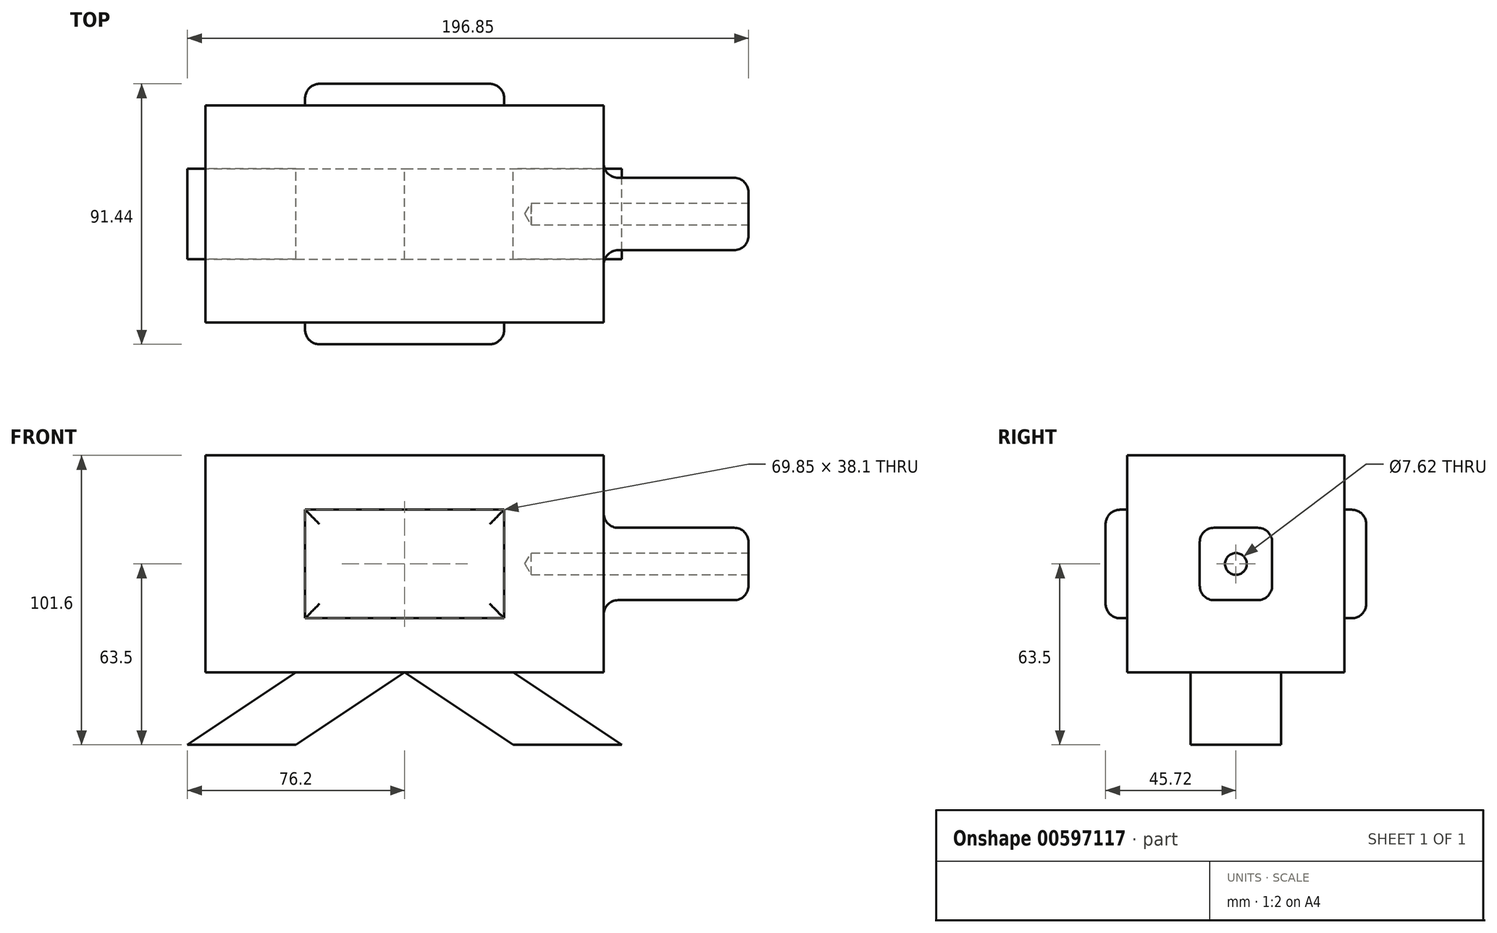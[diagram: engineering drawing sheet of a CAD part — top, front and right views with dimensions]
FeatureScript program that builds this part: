
annotation { "Feature Type Name" : "Feature", "Feature Type Description" : "" }
export const myFeature = defineFeature(function(context is Context, id is Id, definition is map)
    precondition{}
    {
        {
            var Q0;
            Q0=qCreatedBy(makeId("Top.planeOp"),FACE);
            var sketch = newSketch(context, id + "F0", { "sketchPlane" : qUnion([Q0])});
            skLineSegment(sketch, "E0.bottom", {"start": v(69.85, 38.1) * mm, "end": v(-69.85, 38.1) * mm});
            skLineSegment(sketch, "E0.top", {"start": v(69.85, -38.1) * mm, "end": v(-69.85, -38.1) * mm});
            skLineSegment(sketch, "E0.left", {"start": v(69.85, 38.1) * mm, "end": v(69.85, -38.1) * mm});
            skLineSegment(sketch, "E0.right", {"start": v(-69.85, 38.1) * mm, "end": v(-69.85, -38.1) * mm});
            skPoint(sketch, "E0.middle", {"position": v(0, 0) * mm});
            skSolve(sketch);
        }
        {
            var Q0;
            Q0=makeQuery(id+"F0.imprint","IMPRINT",FACE,{"disambiguationData":[TD([[makeQuery(id+"F0.imprint","IMPRINT",EDGE,{"derivedFrom":sQuery(id+"F0.wireOp",EDGE,"E0.bottom")}),1.0]])]});
            extrude(context, id + "F1", {"entities" : qUnion([Q0]), "depth" : 76.2 * mm, "offsetDistance" : 25.4 * mm});
        }
        {
            var Q0;
            Q0=makeQuery(id+"F1.opExtrude","SWEPT_FACE",FACE,{"disambiguationData":[OSD([sQuery(id+"F0.wireOp",EDGE,"E0.left")])]});
            var sketch = newSketch(context, id + "F2", { "sketchPlane" : qUnion([Q0])});
            skLineSegment(sketch, "E1", {"start": v(-38.1, 76.2) * mm, "end": v(38.1, 0) * mm});
            skLineSegment(sketch, "E2", {"start": v(38.1, 0) * mm, "end": v(-38.1, 0) * mm});
            skLineSegment(sketch, "E3", {"start": v(-38.1, 0) * mm, "end": v(38.1, 76.2) * mm});
            skLineSegment(sketch, "E4", {"start": v(0, 38.1) * mm, "end": v(0, 50.8) * mm});
            skPoint(sketch, "E4.endSnap0", {"position": v(0, 38.1) * mm});
            skLineSegment(sketch, "E5", {"start": v(0, 38.1) * mm, "end": v(-12.7, 38.1) * mm});
            skLineSegment(sketch, "E6", {"start": v(0, 38.1) * mm, "end": v(12.7, 38.1) * mm});
            skLineSegment(sketch, "E7", {"start": v(0, 38.1) * mm, "end": v(0, 25.4) * mm});
            skLineSegment(sketch, "E8.bottom", {"start": v(-12.7, 50.8) * mm, "end": v(12.7, 50.8) * mm});
            skLineSegment(sketch, "E8.top", {"start": v(-12.7, 25.4) * mm, "end": v(12.7, 25.4) * mm});
            skLineSegment(sketch, "E8.left", {"start": v(-12.7, 50.8) * mm, "end": v(-12.7, 25.4) * mm});
            skLineSegment(sketch, "E8.right", {"start": v(12.7, 50.8) * mm, "end": v(12.7, 25.4) * mm});
            skSolve(sketch);
        }
        {
            var Q0;
            {var subQ0=sQuery(id+"F2.wireOp",EDGE,"E4");Q0=makeQuery(id+"F2.imprint","IMPRINT",FACE,{"disambiguationData":[TD([[makeQuery(id+"F2.imprint","IMPRINT",EDGE,{"derivedFrom":subQ0}),-1.0]])]});}
            var Q1;
            {var subQ0=sQuery(id+"F2.wireOp",EDGE,"E6");Q1=makeQuery(id+"F2.imprint","IMPRINT",FACE,{"disambiguationData":[TD([[makeQuery(id+"F2.imprint","IMPRINT",EDGE,{"derivedFrom":subQ0}),1.0]])]});}
            var Q2;
            {var subQ0=sQuery(id+"F2.wireOp",EDGE,"E6");Q2=makeQuery(id+"F2.imprint","IMPRINT",FACE,{"disambiguationData":[TD([[makeQuery(id+"F2.imprint","IMPRINT",EDGE,{"derivedFrom":subQ0}),-1.0]])]});}
            var Q3;
            {var subQ0=sQuery(id+"F2.wireOp",EDGE,"E7");Q3=makeQuery(id+"F2.imprint","IMPRINT",FACE,{"disambiguationData":[TD([[makeQuery(id+"F2.imprint","IMPRINT",EDGE,{"derivedFrom":subQ0}),1.0]])]});}
            var Q4;
            {var subQ0=sQuery(id+"F2.wireOp",EDGE,"E7");Q4=makeQuery(id+"F2.imprint","IMPRINT",FACE,{"disambiguationData":[TD([[makeQuery(id+"F2.imprint","IMPRINT",EDGE,{"derivedFrom":subQ0}),-1.0]])]});}
            var Q5;
            {var subQ0=sQuery(id+"F2.wireOp",EDGE,"E5");Q5=makeQuery(id+"F2.imprint","IMPRINT",FACE,{"disambiguationData":[TD([[makeQuery(id+"F2.imprint","IMPRINT",EDGE,{"derivedFrom":subQ0}),1.0]])]});}
            var Q6;
            {var subQ0=sQuery(id+"F2.wireOp",EDGE,"E4");Q6=makeQuery(id+"F2.imprint","IMPRINT",FACE,{"disambiguationData":[TD([[makeQuery(id+"F2.imprint","IMPRINT",EDGE,{"derivedFrom":subQ0}),1.0]])]});}
            var Q7;
            {var subQ0=sQuery(id+"F2.wireOp",EDGE,"E5");Q7=makeQuery(id+"F2.imprint","IMPRINT",FACE,{"disambiguationData":[TD([[makeQuery(id+"F2.imprint","IMPRINT",EDGE,{"derivedFrom":subQ0}),-1.0]])]});}
            extrude(context, id + "F3", {"entities" : qUnion([Q0, Q1, Q2, Q3, Q4, Q5, Q6, Q7]), "operationType" : NewBodyOperationType.ADD, "depth" : 50.8 * mm, "offsetDistance" : 25.4 * mm});
        }
        {
            var Q0;
            Q0=makeQuery(id+"F1.opExtrude","SWEPT_FACE",FACE,{"disambiguationData":[OSD([sQuery(id+"F0.wireOp",EDGE,"E0.top")])]});
            var sketch = newSketch(context, id + "F4", { "sketchPlane" : qUnion([Q0])});
            skLineSegment(sketch, "E9", {"start": v(-69.85, 76.2) * mm, "end": v(69.85, 0) * mm});
            skLineSegment(sketch, "E10", {"start": v(69.85, 0) * mm, "end": v(69.85, 76.2) * mm});
            skLineSegment(sketch, "E11", {"start": v(69.85, 76.2) * mm, "end": v(-69.85, 0) * mm});
            skLineSegment(sketch, "E12.bottom", {"start": v(34.93, 57.15) * mm, "end": v(-34.93, 57.15) * mm});
            skLineSegment(sketch, "E12.top", {"start": v(34.93, 19.05) * mm, "end": v(-34.93, 19.05) * mm});
            skLineSegment(sketch, "E12.left", {"start": v(34.93, 57.15) * mm, "end": v(34.93, 19.05) * mm});
            skLineSegment(sketch, "E12.right", {"start": v(-34.93, 57.15) * mm, "end": v(-34.93, 19.05) * mm});
            skPoint(sketch, "E12.middle", {"position": v(0, 38.1) * mm});
            skSolve(sketch);
        }
        {
            var Q0;
            Q0=makeQuery(id+"F1.opExtrude","SWEPT_FACE",FACE,{"disambiguationData":[OSD([sQuery(id+"F0.wireOp",EDGE,"E0.bottom")])]});
            var sketch = newSketch(context, id + "F5", { "sketchPlane" : qUnion([Q0])});
            skLineSegment(sketch, "E13", {"start": v(-69.85, 76.2) * mm, "end": v(69.85, 0) * mm});
            skLineSegment(sketch, "E14", {"start": v(69.85, 0) * mm, "end": v(-69.85, 0) * mm});
            skLineSegment(sketch, "E15", {"start": v(-69.85, 0) * mm, "end": v(69.85, 76.2) * mm});
            skLineSegment(sketch, "E16.bottom", {"start": v(34.93, 57.15) * mm, "end": v(-34.93, 57.15) * mm});
            skLineSegment(sketch, "E16.top", {"start": v(34.93, 19.05) * mm, "end": v(-34.93, 19.05) * mm});
            skLineSegment(sketch, "E16.left", {"start": v(34.93, 57.15) * mm, "end": v(34.93, 19.05) * mm});
            skLineSegment(sketch, "E16.right", {"start": v(-34.93, 57.15) * mm, "end": v(-34.93, 19.05) * mm});
            skPoint(sketch, "E16.middle", {"position": v(0, 38.1) * mm});
            skSolve(sketch);
        }
        {
            var Q0;
            {var subQ0=sQuery(id+"F5.wireOp",EDGE,"E16.bottom");Q0=makeQuery(id+"F5.imprint","IMPRINT",FACE,{"disambiguationData":[TD([[makeQuery(id+"F5.imprint","IMPRINT",EDGE,{"derivedFrom":subQ0}),1.0]])]});}
            var Q1;
            {var subQ0=sQuery(id+"F5.wireOp",EDGE,"E16.right");Q1=makeQuery(id+"F5.imprint","IMPRINT",FACE,{"disambiguationData":[TD([[makeQuery(id+"F5.imprint","IMPRINT",EDGE,{"derivedFrom":subQ0}),1.0]])]});}
            var Q2;
            {var subQ0=sQuery(id+"F5.wireOp",EDGE,"E16.left");Q2=makeQuery(id+"F5.imprint","IMPRINT",FACE,{"disambiguationData":[TD([[makeQuery(id+"F5.imprint","IMPRINT",EDGE,{"derivedFrom":subQ0}),-1.0]])]});}
            var Q3;
            {var subQ0=sQuery(id+"F5.wireOp",EDGE,"E16.top");Q3=makeQuery(id+"F5.imprint","IMPRINT",FACE,{"disambiguationData":[TD([[makeQuery(id+"F5.imprint","IMPRINT",EDGE,{"derivedFrom":subQ0}),-1.0]])]});}
            extrude(context, id + "F6", {"entities" : qUnion([Q0, Q1, Q2, Q3]), "operationType" : NewBodyOperationType.ADD, "depth" : 7.62 * mm, "offsetDistance" : 25.4 * mm});
        }
        {
            var Q0;
            {var subQ0=sQuery(id+"F4.wireOp",EDGE,"E12.bottom");Q0=makeQuery(id+"F4.imprint","IMPRINT",FACE,{"disambiguationData":[TD([[makeQuery(id+"F4.imprint","IMPRINT",EDGE,{"derivedFrom":subQ0}),1.0]])]});}
            var Q1;
            {var subQ0=sQuery(id+"F4.wireOp",EDGE,"E12.right");Q1=makeQuery(id+"F4.imprint","IMPRINT",FACE,{"disambiguationData":[TD([[makeQuery(id+"F4.imprint","IMPRINT",EDGE,{"derivedFrom":subQ0}),1.0]])]});}
            var Q2;
            {var subQ0=sQuery(id+"F4.wireOp",EDGE,"E12.top");Q2=makeQuery(id+"F4.imprint","IMPRINT",FACE,{"disambiguationData":[TD([[makeQuery(id+"F4.imprint","IMPRINT",EDGE,{"derivedFrom":subQ0}),-1.0]])]});}
            var Q3;
            {var subQ0=sQuery(id+"F4.wireOp",EDGE,"E12.left");Q3=makeQuery(id+"F4.imprint","IMPRINT",FACE,{"disambiguationData":[TD([[makeQuery(id+"F4.imprint","IMPRINT",EDGE,{"derivedFrom":subQ0}),-1.0]])]});}
            extrude(context, id + "F7", {"entities" : qUnion([Q0, Q1, Q2, Q3]), "operationType" : NewBodyOperationType.ADD, "depth" : 7.62 * mm, "offsetDistance" : 25.4 * mm});
        }
        {
            var Q0;
            Q0=makeQuery(id+"F1.opExtrude","CAP_FACE",FACE,{"disambiguationData":[OSD([sQuery(id+"F0.wireOp",EDGE,"E0.bottom"),sQuery(id+"F0.wireOp",EDGE,"E0.top"),sQuery(id+"F0.wireOp",EDGE,"E0.left"),sQuery(id+"F0.wireOp",EDGE,"E0.right")])],"isStart":true});
            var sketch = newSketch(context, id + "F8", { "sketchPlane" : qUnion([Q0])});
            skLineSegment(sketch, "E17.bottom", {"start": v(-38.1, 15.88) * mm, "end": v(38.1, 15.88) * mm});
            skLineSegment(sketch, "E17.top", {"start": v(-38.1, -15.88) * mm, "end": v(38.1, -15.88) * mm});
            skLineSegment(sketch, "E17.left", {"start": v(-38.1, 15.88) * mm, "end": v(-38.1, -15.87) * mm});
            skLineSegment(sketch, "E17.right", {"start": v(38.1, 15.88) * mm, "end": v(38.1, -15.87) * mm});
            skPoint(sketch, "E17.middle", {"position": v(0, 0) * mm});
            skLineSegment(sketch, "E18", {"start": v(0, 15.88) * mm, "end": v(0, -15.88) * mm});
            skSolve(sketch);
        }
        {
            var Q0;
            {var subQ0=sQuery(id+"F8.wireOp",EDGE,"E17.right");Q0=makeQuery(id+"F8.imprint","IMPRINT",FACE,{"disambiguationData":[TD([[makeQuery(id+"F8.imprint","IMPRINT",EDGE,{"derivedFrom":subQ0}),-1.0]])]});}
            cPlane(context, id + "F9", {"entities" : qUnion([Q0]), "cplaneType" : CPlaneType.OFFSET, "offset" : 25.4 * mm, "width" : 152.4 * mm, "height" : 152.4 * mm});
        }
        {
            var Q0;
            Q0=qCreatedBy(id+"F9.planeOp",FACE);
            var sketch = newSketch(context, id + "F10", { "sketchPlane" : qUnion([Q0])});
            skLineSegment(sketch, "E19.left", {"start": v(76.2, 15.88) * mm, "end": v(76.2, -15.88) * mm});
            skLineSegment(sketch, "E19.right", {"start": v(-76.2, 15.88) * mm, "end": v(-76.2, -15.88) * mm});
            skPoint(sketch, "E19.middle", {"position": v(0, 0) * mm});
            skLineSegment(sketch, "E20", {"start": v(-38.1, 0) * mm, "end": v(-38.1, 15.88) * mm});
            skLineSegment(sketch, "E21", {"start": v(-38.1, 15.88) * mm, "end": v(-38.1, 0) * mm});
            skLineSegment(sketch, "E22", {"start": v(-38.1, -15.88) * mm, "end": v(-38.1, 0) * mm});
            skLineSegment(sketch, "E23", {"start": v(38.1, 0) * mm, "end": v(38.1, 15.88) * mm});
            skLineSegment(sketch, "E24", {"start": v(38.1, 15.88) * mm, "end": v(38.1, 0) * mm});
            skLineSegment(sketch, "E25", {"start": v(38.1, -15.88) * mm, "end": v(38.1, 0) * mm});
            skPoint(sketch, "E26", {"position": v(-38.1, -15.88) * mm});
            skPoint(sketch, "E27", {"position": v(38.1, -15.88) * mm});
            skLineSegment(sketch, "E28", {"start": v(-76.2, -15.88) * mm, "end": v(-38.1, -15.88) * mm});
            skLineSegment(sketch, "E29", {"start": v(38.1, -15.88) * mm, "end": v(76.2, -15.88) * mm});
            skLineSegment(sketch, "E30", {"start": v(-76.2, 15.88) * mm, "end": v(-38.1, 15.88) * mm});
            skLineSegment(sketch, "E31", {"start": v(38.1, 15.88) * mm, "end": v(76.2, 15.88) * mm});
            skSolve(sketch);
        }
        {
            var Q1;
            Q1=makeQuery(id+"F10.imprint","IMPRINT",FACE,{"disambiguationData":[TD([[makeQuery(id+"F10.imprint","IMPRINT",EDGE,{"derivedFrom":sQuery(id+"F10.wireOp",EDGE,"E19.left")}),-1.0]])]});
            var Q2;
            {var subQ0=sQuery(id+"F8.wireOp",EDGE,"E17.right");Q2=makeQuery(id+"F8.imprint","IMPRINT",FACE,{"disambiguationData":[TD([[makeQuery(id+"F8.imprint","IMPRINT",EDGE,{"derivedFrom":subQ0}),-1.0]])]});}
            loft(context, id + "F11", {"operationType" : NewBodyOperationType.ADD, "sheetProfilesArray" : [{ "sheetProfileEntities" : qUnion([Q1]) }, { "sheetProfileEntities" : qUnion([Q2]) }]});
        }
        {
            var Q1;
            {var subQ0=sQuery(id+"F8.wireOp",EDGE,"E17.left");Q1=makeQuery(id+"F8.imprint","IMPRINT",FACE,{"disambiguationData":[TD([[makeQuery(id+"F8.imprint","IMPRINT",EDGE,{"derivedFrom":subQ0}),1.0]])]});}
            var Q2;
            Q2=makeQuery(id+"F10.imprint","IMPRINT",FACE,{"disambiguationData":[TD([[makeQuery(id+"F10.imprint","IMPRINT",EDGE,{"derivedFrom":sQuery(id+"F10.wireOp",EDGE,"E19.right")}),1.0]])]});
            loft(context, id + "F12", {"operationType" : NewBodyOperationType.ADD, "sheetProfilesArray" : [{ "sheetProfileEntities" : qUnion([Q1]) }, { "sheetProfileEntities" : qUnion([Q2]) }]});
        }
        {
            var Q0;
            Q0=makeQuery(id+"F3.opExtrude","SWEPT_FACE",FACE,{"disambiguationData":[OSD([sQuery(id+"F2.wireOp",EDGE,"E8.left")])]});
            var Q1;
            Q1=makeQuery(id+"F3.opExtrude","SWEPT_FACE",FACE,{"disambiguationData":[OSD([sQuery(id+"F2.wireOp",EDGE,"E8.bottom")])]});
            var Q2;
            Q2=makeQuery(id+"F3.opExtrude","SWEPT_FACE",FACE,{"disambiguationData":[OSD([sQuery(id+"F2.wireOp",EDGE,"E8.right")])]});
            var Q3;
            Q3=makeQuery(id+"F3.opExtrude","SWEPT_FACE",FACE,{"disambiguationData":[OSD([sQuery(id+"F2.wireOp",EDGE,"E8.top")])]});
            fillet(context, id + "F13", {"entities" : qUnion([Q0, Q1, Q2, Q3]), "radius" : 5.08 * mm, "tangentPropagation" : true, "allowEdgeOverflow" : false});
        }
        {
            var Q0;
            Q0=makeQuery(id+"F6.opExtrude","CAP_FACE",FACE,{"disambiguationData":[OSD([sQuery(id+"F5.wireOp",EDGE,"E16.bottom"),sQuery(id+"F5.wireOp",EDGE,"E16.top"),sQuery(id+"F5.wireOp",EDGE,"E16.left"),sQuery(id+"F5.wireOp",EDGE,"E16.right")])],"isStart":false});
            fillet(context, id + "F14", {"entities" : qUnion([Q0]), "radius" : 5.08 * mm, "tangentPropagation" : true, "allowEdgeOverflow" : false});
        }
        {
            var Q0;
            Q0=makeQuery(id+"F7.opExtrude","CAP_FACE",FACE,{"disambiguationData":[OSD([sQuery(id+"F4.wireOp",EDGE,"E12.bottom"),sQuery(id+"F4.wireOp",EDGE,"E12.top"),sQuery(id+"F4.wireOp",EDGE,"E12.left"),sQuery(id+"F4.wireOp",EDGE,"E12.right")])],"isStart":false});
            fillet(context, id + "F15", {"entities" : qUnion([Q0]), "radius" : 5.08 * mm, "tangentPropagation" : true, "allowEdgeOverflow" : false});
        }
        {
            var Q0;
            Q0=makeQuery(id+"F3.opExtrude","CAP_FACE",FACE,{"disambiguationData":[OSD([sQuery(id+"F2.wireOp",EDGE,"E8.bottom"),sQuery(id+"F2.wireOp",EDGE,"E8.top"),sQuery(id+"F2.wireOp",EDGE,"E8.left"),sQuery(id+"F2.wireOp",EDGE,"E8.right")])],"isStart":false});
            var sketch = newSketch(context, id + "F16", { "sketchPlane" : qUnion([Q0])});
            skLineSegment(sketch, "E32", {"start": v(-7.62, 45.72) * mm, "end": v(7.62, 30.48) * mm});
            skLineSegment(sketch, "E33", {"start": v(7.62, 30.48) * mm, "end": v(-7.62, 30.48) * mm});
            skLineSegment(sketch, "E34", {"start": v(-7.62, 30.48) * mm, "end": v(7.62, 45.72) * mm});
            skPoint(sketch, "E35", {"position": v(0, 38.1) * mm});
            skSolve(sketch);
        }
        {
            var Q0;
            Q0=sQuery(id+"F16.wireOp",VERTEX,"E35");
            var Q1;
            Q1=makeQuery(id+"F1.opExtrude","SWEPT_BODY",BODY,{"disambiguationData":[OSD([sQuery(id+"F0.wireOp",EDGE,"E0.bottom"),sQuery(id+"F0.wireOp",EDGE,"E0.top"),sQuery(id+"F0.wireOp",EDGE,"E0.left"),sQuery(id+"F0.wireOp",EDGE,"E0.right")])]});
            hole(context, id + "F17", {"style" : HoleStyle.SIMPLE, "endStyle" : HoleEndStyle.BLIND, "holeDiameter" : 7.62 * mm, "majorDiameter" : 6.35 * mm, "holeDepth" : 76.2 * mm, "isTappedThrough" : true, "tappedDepth" : 12.7 * mm, "tapClearance" : 3, "locations" : qUnion([Q0]), "scope" : qUnion([Q1])});
        }
    });
